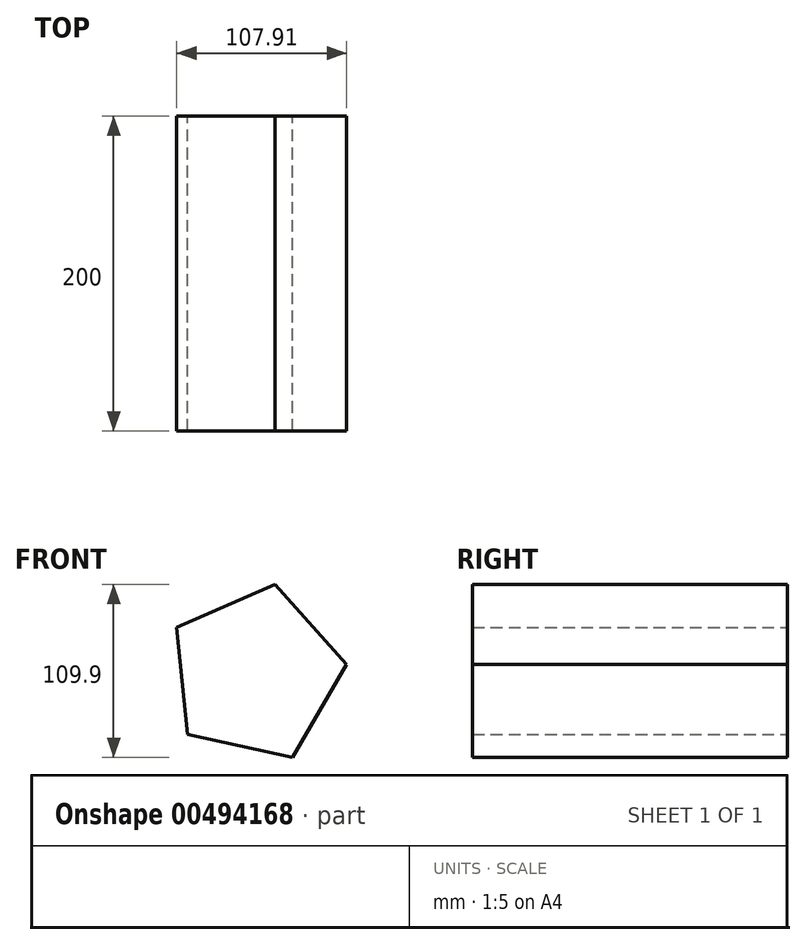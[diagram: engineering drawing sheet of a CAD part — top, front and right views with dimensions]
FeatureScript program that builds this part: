
annotation { "Feature Type Name" : "Feature", "Feature Type Description" : "" }
export const myFeature = defineFeature(function(context is Context, id is Id, definition is map)
    precondition{}
    {
        {
            var Q0;
            Q0=qCreatedBy(makeId("Front.planeOp"),FACE);
            var sketch = newSketch(context, id + "F0", { "sketchPlane" : qUnion([Q0])});
            skCircle(sketch, "E0.cCircle", {"center": v(0, 0) * mm, "radius": 58.06 * mm, "construction": true});
            skLineSegment(sketch, "E0.0", {"start": v(-50.13, 29.3) * mm, "end": v(12.37, 56.73) * mm});
            skLineSegment(sketch, "E0.1", {"start": v(12.37, 56.73) * mm, "end": v(57.78, 5.77) * mm});
            skLineSegment(sketch, "E0.2", {"start": v(57.78, 5.77) * mm, "end": v(23.34, -53.17) * mm});
            skLineSegment(sketch, "E0.3", {"start": v(23.34, -53.17) * mm, "end": v(-43.35, -38.63) * mm});
            skLineSegment(sketch, "E0.4", {"start": v(-43.35, -38.63) * mm, "end": v(-50.13, 29.3) * mm});
            skSolve(sketch);
        }
        {
            var Q0;
            Q0=makeQuery(id+"F0.imprint","IMPRINT",FACE,{"disambiguationData":[TD([[makeQuery(id+"F0.imprint","IMPRINT",EDGE,{"derivedFrom":sQuery(id+"F0.wireOp",EDGE,"E0.0")}),-1.0]])]});
            extrude(context, id + "F1", {"entities" : qUnion([Q0]), "endBound" : BoundingType.SYMMETRIC, "depth" : 200 * mm});
        }
    });
